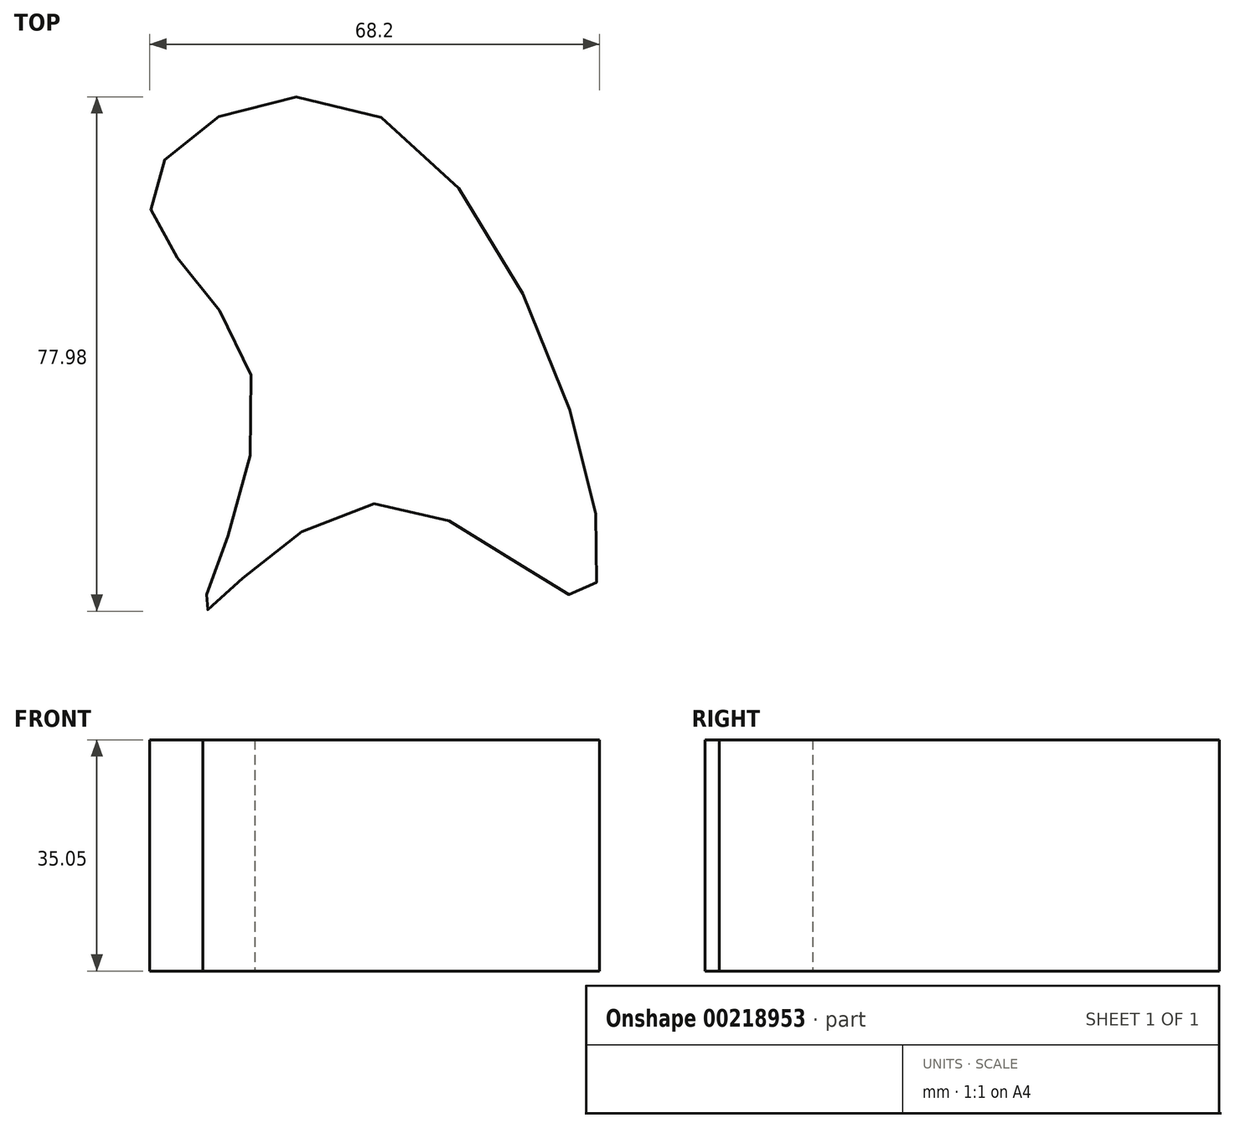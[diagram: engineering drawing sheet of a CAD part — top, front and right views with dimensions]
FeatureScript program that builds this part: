
annotation { "Feature Type Name" : "Feature", "Feature Type Description" : "" }
export const myFeature = defineFeature(function(context is Context, id is Id, definition is map)
    precondition{}
    {
        {
            var Q0;
            Q0=qCreatedBy(makeId("Top.planeOp"),FACE);
            var sketch = newSketch(context, id + "F0", { "sketchPlane" : qUnion([Q0])});
            skFitSpline(sketch, "E0", {"points": [v(0, 40.57) * mm, v(-35.01, 29.09) * mm, v(-19.45, 0) * mm, v(-26.86, -34.27) * mm, v(0, -17.97) * mm, v(31.68, -31.68) * mm, v(0, 40.57) * mm]});
            skSolve(sketch);
        }
        {
            var Q0;
            Q0=makeQuery(id+"F0.imprint","IMPRINT",FACE,{"disambiguationData":[TD([[makeQuery(id+"F0.imprint","IMPRINT",EDGE,{"derivedFrom":sQuery(id+"F0.wireOp",EDGE,"E0")}),1.0]])]});
            extrude(context, id + "F1", {"entities" : qUnion([Q0]), "depth" : 35.05 * mm});
        }
    });
